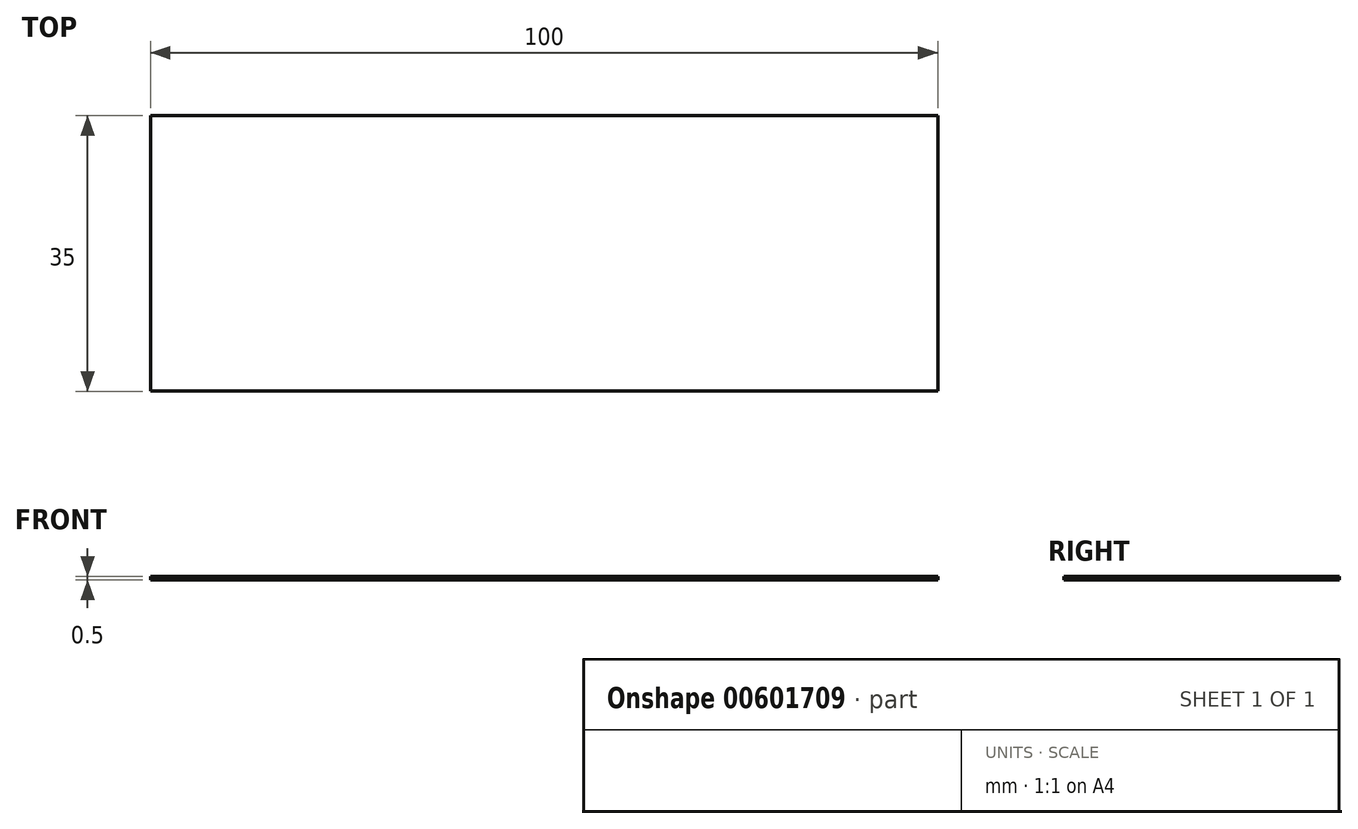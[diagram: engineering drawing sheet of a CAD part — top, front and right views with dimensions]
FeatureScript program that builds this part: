
annotation { "Feature Type Name" : "Feature", "Feature Type Description" : "" }
export const myFeature = defineFeature(function(context is Context, id is Id, definition is map)
    precondition{}
    {
        {
            var Q0;
            Q0=qCreatedBy(makeId("Top.planeOp"),FACE);
            var sketch = newSketch(context, id + "F0", { "sketchPlane" : qUnion([Q0])});
            skLineSegment(sketch, "E0.bottom", {"start": v(-67.92, 26.47) * mm, "end": v(32.08, 26.47) * mm});
            skLineSegment(sketch, "E0.top", {"start": v(-67.92, -8.53) * mm, "end": v(32.08, -8.53) * mm});
            skLineSegment(sketch, "E0.left", {"start": v(-67.92, 26.47) * mm, "end": v(-67.92, -8.53) * mm});
            skLineSegment(sketch, "E0.right", {"start": v(32.08, 26.47) * mm, "end": v(32.08, -8.53) * mm});
            skSolve(sketch);
        }
        {
            var Q0;
            Q0=makeQuery(id+"F0.imprint","IMPRINT",FACE,{"disambiguationData":[TD([[makeQuery(id+"F0.imprint","IMPRINT",EDGE,{"derivedFrom":sQuery(id+"F0.wireOp",EDGE,"E0.bottom")}),-1.0]])]});
            extrude(context, id + "F1", {"entities" : qUnion([Q0]), "depth" : .5 * mm, "offsetDistance" : 25 * mm});
        }
    });
